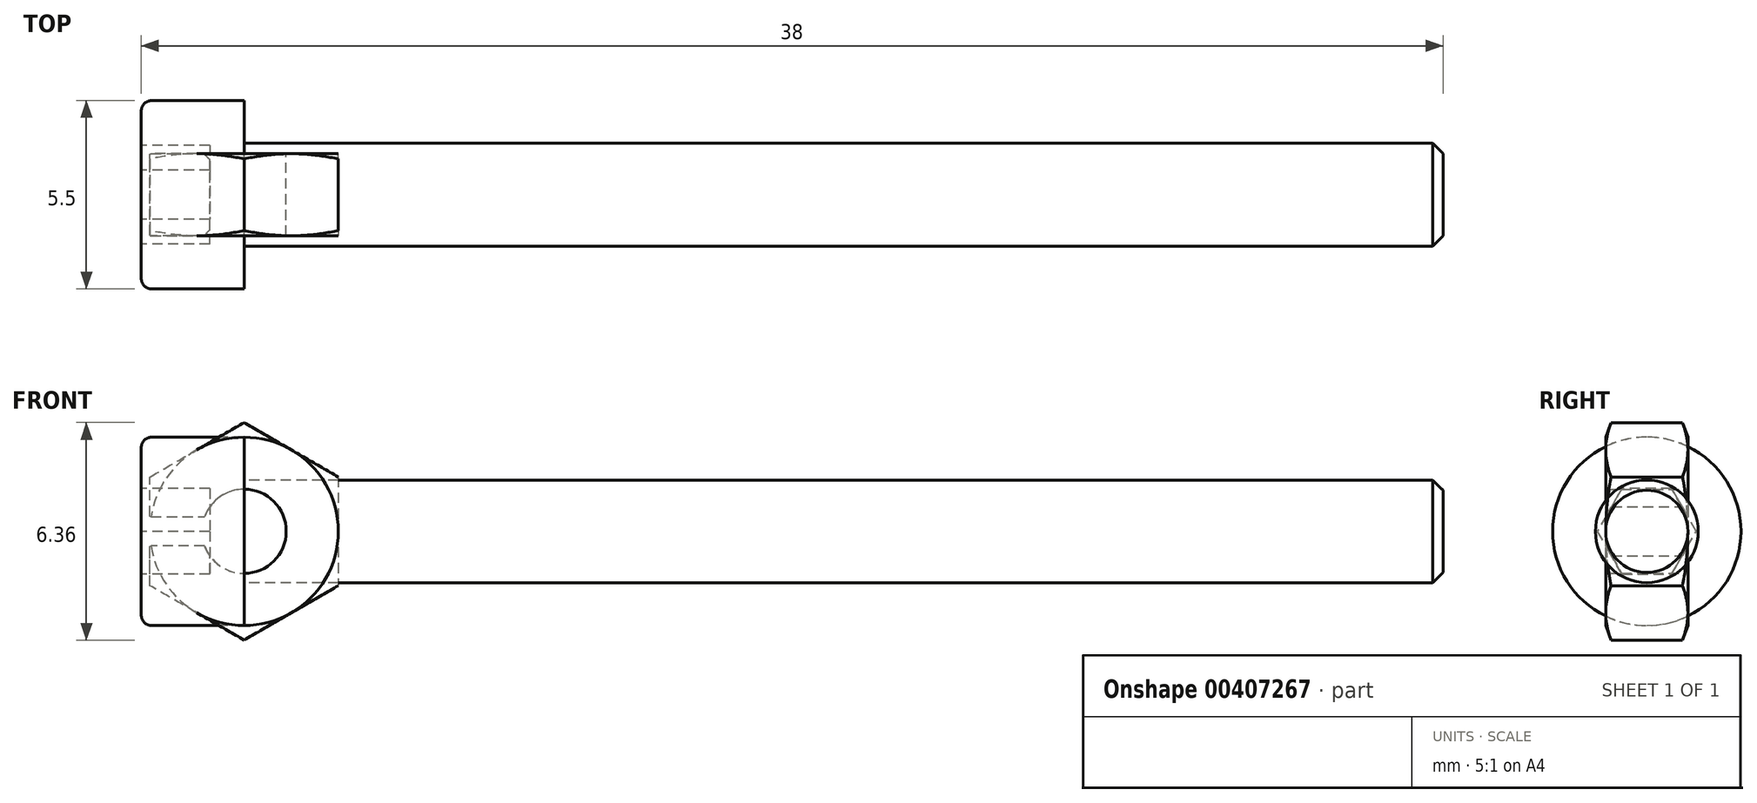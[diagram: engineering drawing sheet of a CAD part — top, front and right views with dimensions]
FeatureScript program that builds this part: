
annotation { "Feature Type Name" : "Feature", "Feature Type Description" : "" }
export const myFeature = defineFeature(function(context is Context, id is Id, definition is map)
    precondition{}
    {
        {
            var Q0;
            Q0=qCreatedBy(makeId("Front.planeOp"),FACE);
            var sketch = newSketch(context, id + "F0", { "sketchPlane" : qUnion([Q0])});
            skCircle(sketch, "E0.cCircle", {"center": v(0, 0) * mm, "radius": 3.18 * mm, "construction": true});
            skLineSegment(sketch, "E0.0", {"start": v(0, -3.18) * mm, "end": v(-2.75, -1.59) * mm});
            skLineSegment(sketch, "E0.1", {"start": v(-2.75, -1.59) * mm, "end": v(-2.75, 1.59) * mm});
            skLineSegment(sketch, "E0.2", {"start": v(-2.75, 1.59) * mm, "end": v(0, 3.18) * mm});
            skLineSegment(sketch, "E0.3", {"start": v(0, 3.18) * mm, "end": v(2.75, 1.59) * mm});
            skLineSegment(sketch, "E0.4", {"start": v(2.75, 1.59) * mm, "end": v(2.75, -1.59) * mm});
            skLineSegment(sketch, "E0.5", {"start": v(2.75, -1.59) * mm, "end": v(0, -3.18) * mm});
            skSolve(sketch);
        }
        {
            var Q0;
            Q0=makeQuery(id+"F0.imprint","IMPRINT",FACE,{"disambiguationData":[TD([[makeQuery(id+"F0.imprint","IMPRINT",EDGE,{"derivedFrom":sQuery(id+"F0.wireOp",EDGE,"E0.0")}),-1.0]])]});
            extrude(context, id + "F1", {"entities" : qUnion([Q0]), "endBound" : BoundingType.SYMMETRIC, "oppositeDirection" : true, "depth" : 2.4 * mm});
        }
        {
            var Q0;
            Q0=qCreatedBy(makeId("Top.planeOp"),FACE);
            var sketch = newSketch(context, id + "F2", { "sketchPlane" : qUnion([Q0])});
            skLineSegment(sketch, "E1.0", {"start": v(0, 1.2) * mm, "end": v(0, -1.2) * mm, "construction": true});
            skLineSegment(sketch, "E2", {"start": v(2.75, 1.2) * mm, "end": v(5, 0.38) * mm});
            skLineSegment(sketch, "E3", {"start": v(5, 0.38) * mm, "end": v(5, -0.38) * mm});
            skLineSegment(sketch, "E4", {"start": v(5, -0.38) * mm, "end": v(2.75, -1.2) * mm});
            skLineSegment(sketch, "E5", {"start": v(2.75, 1.2) * mm, "end": v(2.75, 2.2) * mm});
            skLineSegment(sketch, "E6", {"start": v(2.75, 2.2) * mm, "end": v(5.75, 2.2) * mm});
            skLineSegment(sketch, "E7", {"start": v(5.75, 2.2) * mm, "end": v(5.75, -2.2) * mm});
            skLineSegment(sketch, "E8", {"start": v(5.75, -2.2) * mm, "end": v(2.75, -2.2) * mm});
            skLineSegment(sketch, "E9", {"start": v(2.75, -2.2) * mm, "end": v(2.75, -1.2) * mm});
            skSolve(sketch);
        }
        {
            var Q0;
            Q0=makeQuery(id+"F2.imprint","IMPRINT",FACE,{"disambiguationData":[TD([[makeQuery(id+"F2.imprint","IMPRINT",EDGE,{"derivedFrom":sQuery(id+"F2.wireOp",EDGE,"E2")}),1.0]])]});
            var Q1;
            Q1=sQuery(id+"F2.wireOp",EDGE,"E1.0");
            revolve(context, id + "F3", {"operationType" : NewBodyOperationType.REMOVE, "entities" : qUnion([Q0]), "axis" : qUnion([Q1]), "revolveType" : RevolveType.FULL, "oppositeDirection" : true});
        }
        {
            var Q0;
            Q0=makeQuery(id+"F1.opExtrude","CAP_FACE",FACE,{"disambiguationData":[OSD([sQuery(id+"F0.wireOp",EDGE,"E0.0"),sQuery(id+"F0.wireOp",EDGE,"E0.1"),sQuery(id+"F0.wireOp",EDGE,"E0.2"),sQuery(id+"F0.wireOp",EDGE,"E0.3"),sQuery(id+"F0.wireOp",EDGE,"E0.4"),sQuery(id+"F0.wireOp",EDGE,"E0.5")])],"isStart":false});
            var sketch = newSketch(context, id + "F4", { "sketchPlane" : qUnion([Q0])});
            skPoint(sketch, "E10", {"position": v(0, 0) * mm});
            skSolve(sketch);
        }
        {
            var Q0;
            Q0=sQuery(id+"F4.wireOp",VERTEX,"E10");
            var Q1;
            Q1=makeQuery(id+"F1.opExtrude","SWEPT_BODY",BODY,{"disambiguationData":[OSD([sQuery(id+"F0.wireOp",EDGE,"E0.0"),sQuery(id+"F0.wireOp",EDGE,"E0.1"),sQuery(id+"F0.wireOp",EDGE,"E0.2"),sQuery(id+"F0.wireOp",EDGE,"E0.3"),sQuery(id+"F0.wireOp",EDGE,"E0.4"),sQuery(id+"F0.wireOp",EDGE,"E0.5")])]});
            hole(context, id + "F5", {"style" : HoleStyle.SIMPLE, "endStyle" : HoleEndStyle.THROUGH, "holeDiameter" : 2.46 * mm, "isTappedThrough" : true, "tappedDepth" : 12 * mm, "tapClearance" : 3, "locations" : qUnion([Q0]), "scope" : qUnion([Q1])});
        }
        {
            var Q0;
            Q0=qCreatedBy(makeId("Front.planeOp"),FACE);
            var sketch = newSketch(context, id + "F6", { "sketchPlane" : qUnion([Q0])});
            skLineSegment(sketch, "E11", {"start": v(-3, 0) * mm, "end": v(35, 0) * mm, "construction": true});
            skLineSegment(sketch, "E12", {"start": v(35, 0) * mm, "end": v(35, 1.5) * mm});
            skLineSegment(sketch, "E13", {"start": v(35, 1.5) * mm, "end": v(0, 1.5) * mm});
            skLineSegment(sketch, "E14", {"start": v(0, 1.5) * mm, "end": v(0, 2.75) * mm});
            skLineSegment(sketch, "E15", {"start": v(0, 2.75) * mm, "end": v(-3, 2.75) * mm});
            skLineSegment(sketch, "E16", {"start": v(-3, 2.75) * mm, "end": v(-3, 0) * mm});
            skLineSegment(sketch, "E17", {"start": v(-3, 0) * mm, "end": v(35, 0) * mm});
            skSolve(sketch);
        }
        {
            var Q0;
            Q0=makeQuery(id+"F6.imprint","IMPRINT",FACE,{"disambiguationData":[TD([[makeQuery(id+"F6.imprint","IMPRINT",EDGE,{"derivedFrom":sQuery(id+"F6.wireOp",EDGE,"E12")}),1.0]])]});
            var Q1;
            Q1=sQuery(id+"F6.wireOp",EDGE,"E17");
            revolve(context, id + "F7", {"entities" : qUnion([Q0]), "axis" : qUnion([Q1]), "revolveType" : RevolveType.FULL});
        }
        {
            var Q0;
            Q0=makeQuery(id+"F7.opRevolve","SWEPT_EDGE",EDGE,{"disambiguationData":[OSD([sQuery(id+"F6.wireOp",EDGE,"E15"),sQuery(id+"F6.wireOp",EDGE,"E16")])]});
            fillet(context, id + "F8", {"entities" : qUnion([Q0]), "radius" : .3 * mm, "tangentPropagation" : true, "allowEdgeOverflow" : false});
        }
        {
            var Q0;
            Q0=makeQuery(id+"F7.opRevolve","SWEPT_FACE",FACE,{"disambiguationData":[OSD([sQuery(id+"F6.wireOp",EDGE,"E16")])]});
            var sketch = newSketch(context, id + "F9", { "sketchPlane" : qUnion([Q0])});
            skCircle(sketch, "E18.cCircle", {"center": v(0, 0) * mm, "radius": 1.44 * mm, "construction": true});
            skLineSegment(sketch, "E18.0", {"start": v(1.44, 0) * mm, "end": v(0.72, -1.25) * mm});
            skLineSegment(sketch, "E18.1", {"start": v(0.72, -1.25) * mm, "end": v(-0.72, -1.25) * mm});
            skLineSegment(sketch, "E18.2", {"start": v(-0.72, -1.25) * mm, "end": v(-1.44, 0) * mm});
            skLineSegment(sketch, "E18.3", {"start": v(-1.44, 0) * mm, "end": v(-0.72, 1.25) * mm});
            skLineSegment(sketch, "E18.4", {"start": v(-0.72, 1.25) * mm, "end": v(0.72, 1.25) * mm});
            skLineSegment(sketch, "E18.5", {"start": v(0.72, 1.25) * mm, "end": v(1.44, 0) * mm});
            skSolve(sketch);
        }
        {
            var Q0;
            Q0=makeQuery(id+"F9.imprint","IMPRINT",FACE,{"disambiguationData":[TD([[makeQuery(id+"F9.imprint","IMPRINT",EDGE,{"derivedFrom":sQuery(id+"F9.wireOp",EDGE,"E18.0")}),-1.0]])]});
            extrude(context, id + "F10", {"entities" : qUnion([Q0]), "operationType" : NewBodyOperationType.REMOVE, "oppositeDirection" : true, "depth" : 2 * mm});
        }
        {
            var Q0;
            Q0=makeQuery(id+"F7.opRevolve","SWEPT_EDGE",EDGE,{"disambiguationData":[OSD([sQuery(id+"F6.wireOp",EDGE,"E12"),sQuery(id+"F6.wireOp",EDGE,"E13")])]});
            chamfer(context, id + "F11", {"entities" : qUnion([Q0]), "width" : .3 * mm, "tangentPropagation" : true});
        }
    });
